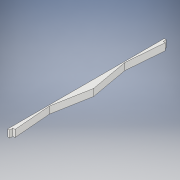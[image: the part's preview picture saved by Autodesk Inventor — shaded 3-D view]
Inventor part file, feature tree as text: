
AUTODESK INVENTOR PART (.ipt)
format: ipt  version: 2017 (Build 210142000, 142)  size: 121,856 bytes
history: native  units: in
note: dims shown in document units (in); Inventor stores cm internally (conversion verified against a paired STEP export)
features: extrude x3, sketch x3
ambient origin geometry x8: Origin, YZ Plane, XZ Plane, XY Plane, X Axis, Y Axis, Z Axis, Center Point
bodies: Solid1 (feature_tree)
feature tree (6):
  extrude  "Extrusion1"  Depth=0.134in
  sketch  "Sketch2"  dims[d2=0.134in d3=1.2285in]
  extrude  "Extrusion2"  Depth=0.134in
  extrude  "Extrusion3"  Depth=1.229in
  sketch  "Sketch1"  dims[d0=4.931in d1=0.134in]
  sketch  "Sketch3"  dims[d4=2.457in d5=1.229in d6=0.229in d7=0.0in d8=0.065in d9=0.065in d10=0.101in d11=0.0in d12=0.101in d13=0.0in d15=0.259in d16=0.035in d17=0.035in]
